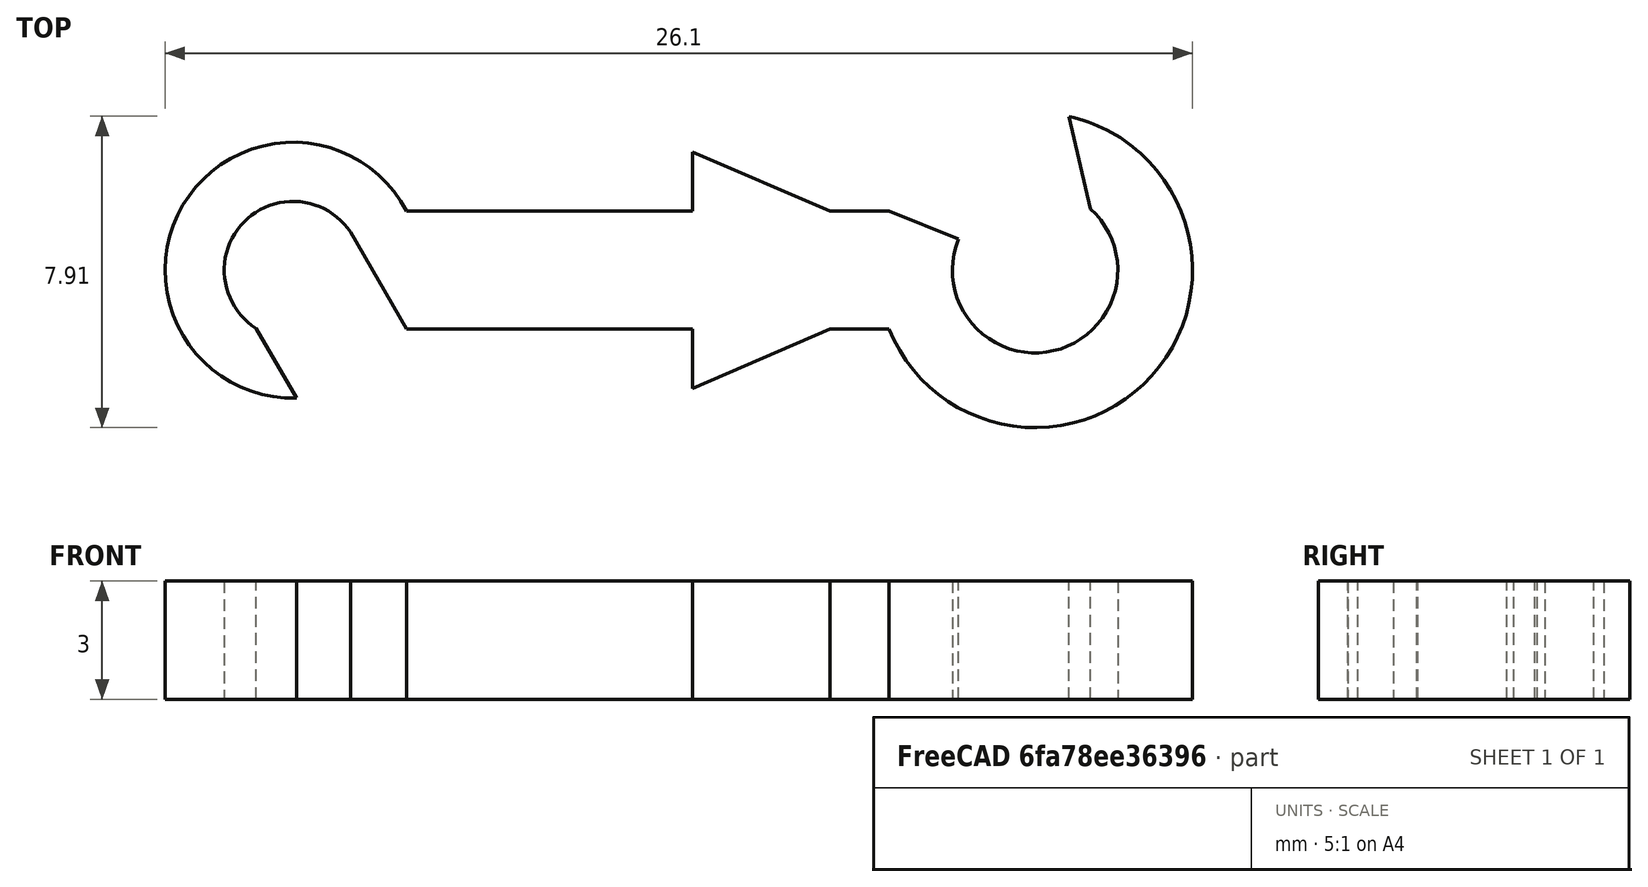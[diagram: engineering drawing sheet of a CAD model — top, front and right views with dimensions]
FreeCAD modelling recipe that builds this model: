
FCSTD DOCUMENT  (FreeCAD 0.20RUnknown)
Label: Haken01
License: All rights reserved
LicenseURL: http://en.wikipedia.org/wiki/All_rights_reserved
objects: Sketcher::SketchObject×1, PartDesign::Pad×1, PartDesign::Body×1
note: 4 computed .brp shape members not serialized (recipe doc carries the construction recipe); baked Part::Feature solids carry a one-line shape summary decoded from their .brp

FEATURE [Sketcher::SketchObject] Sketch
  FullyConstrained = true
  MapMode = 5
  Support = -> [XY_Plane]
  sketch-geometry (31):
    g0: Circle CenterX=0 CenterY=0 CenterZ=0 NormalX=0 NormalY=0 NormalZ=1 AngleXU=0 Radius=1.75
    g1: Circle CenterX=18.85 CenterY=0 CenterZ=0 NormalX=0 NormalY=0 NormalZ=1 AngleXU=0 Radius=2.1
    g2: LineSegment StartX=1.75 StartY=0 StartZ=0 EndX=16.75 EndY=0 EndZ=0
    g3: ArcOfCircle CenterX=18.85 CenterY=0 CenterZ=0 NormalX=0 NormalY=0 NormalZ=1 AngleXU=0 Radius=4 StartAngle=3.52599 EndAngle=7.12052
    g4: ArcOfCircle CenterX=18.85 CenterY=0 CenterZ=0 NormalX=0 NormalY=0 NormalZ=1 AngleXU=0 Radius=2.1 StartAngle=2.7572 EndAngle=7.12052
    g5: ArcOfCircle CenterX=0 CenterY=0 CenterZ=0 NormalX=0 NormalY=0 NormalZ=1 AngleXU=0 Radius=1.75 StartAngle=0.583388 EndAngle=4.14659
    g6: ArcOfCircle CenterX=0 CenterY=0 CenterZ=0 NormalX=0 NormalY=0 NormalZ=1 AngleXU=0 Radius=3.25 StartAngle=0.479729 EndAngle=4.73845
    g7: LineSegment StartX=18.85 StartY=0 StartZ=0 EndX=16.9032 EndY=0.7875 EndZ=0
    g8: LineSegment StartX=16.9032 StartY=0.7875 StartZ=0 EndX=15.1419 EndY=1.5 EndZ=0
    g9: LineSegment StartX=18.85 StartY=0 StartZ=0 EndX=20.2558 EndY=1.56001 EndZ=0
    g10: LineSegment StartX=20.2558 StartY=1.56001 StartZ=0 EndX=21.5278 EndY=2.97144 EndZ=0
    g11: LineSegment StartX=0 StartY=0 StartZ=0 EndX=-1.625 EndY=2.81458 EndZ=0
    g12: LineSegment StartX=2.88314 StartY=-1.5 StartZ=0 EndX=1.46055 EndY=0.963995 EndZ=0
    g13: LineSegment StartX=0.0846838 StartY=-3.2489 StartZ=0 EndX=-0.938159 EndY=-1.47728 EndZ=0
    g14: LineSegment StartX=2.88314 StartY=1.5 StartZ=0 EndX=2.88314 EndY=-1.5 EndZ=0
    g15: LineSegment StartX=15.1419 StartY=1.5 StartZ=0 EndX=15.1419 EndY=0 EndZ=0
    g16: LineSegment StartX=15.1419 StartY=0 StartZ=0 EndX=15.1419 EndY=-1.5 EndZ=0
    g17: LineSegment StartX=13.6419 StartY=1.5 StartZ=0 EndX=10.1419 EndY=3 EndZ=0
    g18: LineSegment StartX=10.1419 StartY=3 StartZ=0 EndX=10.1419 EndY=1.5 EndZ=0
    g19: LineSegment StartX=13.6419 StartY=-1.5 StartZ=0 EndX=10.1419 EndY=-3 EndZ=0
    g20: LineSegment StartX=10.1419 StartY=-3 StartZ=0 EndX=10.1419 EndY=-1.5 EndZ=0
    g21: LineSegment StartX=10.1419 StartY=1.5 StartZ=0 EndX=10.1419 EndY=-1.5 EndZ=0
    g22: LineSegment StartX=13.6419 StartY=1.5 StartZ=0 EndX=13.6419 EndY=-1.5 EndZ=0
    g23: LineSegment StartX=10.1419 StartY=1.5 StartZ=0 EndX=2.88314 EndY=1.5 EndZ=0
    g24: LineSegment StartX=15.1419 StartY=1.5 StartZ=0 EndX=13.6419 EndY=1.5 EndZ=0
    g25: LineSegment StartX=13.6419 StartY=1.5 StartZ=0 EndX=10.1419 EndY=1.5 EndZ=0
    g26: LineSegment StartX=10.1419 StartY=-1.5 StartZ=0 EndX=2.88314 EndY=-1.5 EndZ=0
    g27: LineSegment StartX=15.1419 StartY=-1.5 StartZ=0 EndX=13.6419 EndY=-1.5 EndZ=0
    g28: LineSegment StartX=13.6419 StartY=-1.5 StartZ=0 EndX=10.1419 EndY=-1.5 EndZ=0
    g29: LineSegment StartX=20.2558 StartY=1.56001 StartZ=0 EndX=19.7154 EndY=3.90525 EndZ=0
    g30: ArcOfCircle CenterX=18.85 CenterY=0 CenterZ=0 NormalX=0 NormalY=0 NormalZ=1 AngleXU=0 Radius=4 StartAngle=0.837334 EndAngle=1.35271
  constraints (89):
    c: Diameter(g0) = 3.5
    c: PointOnObject(g1,g-1)
    c: PointOnObject(g2,g0)
    c: PointOnObject(g2,g1)
    c: Horizontal(g2)
    c: PointOnObject(g2,g-1)
    c: DistanceX(g2,g2) = 15
    c: Coincident(g27,g3)
    c: Coincident(g4,g3)
    c: Coincident(g5,g0)
    c: Equal(g1,g4)
    c: Equal(g0,g5)
    c: Coincident(g6,g5)
    c: Coincident(g6,g23)
    c: Coincident(g3,g1)
    c: Coincident(g7,g3)
    c: Coincident(g8,g24)
    c: Coincident(g7,g8)
    c: Parallel(g7,g8)
    c: Coincident(g9,g3)
    c: Coincident(g9,g10)
    c: Parallel(g10,g9)
    c: Angle(g9,g7) = 1.91986
    c: Diameter(g6) = 6.5
    c: Diameter(g3) = 8
    c: DistanceY(g26,g23) = 3
    c: Coincident(g3,g10)
    c: Coincident(g4,g9)
    c: Coincident(g4,g7)
    c: Coincident(g11,g5)
    c: Coincident(g12,g26)
    c: Parallel(g11,g13)
    c: Parallel(g12,g11)
    c: Coincident(g14,g23)
    c: Coincident(g14,g26)
    c: Vertical(g14)
    c: Distance(g13,g26) = 3.3
    c: Coincident(g5,g13)
    c: Coincident(g6,g13)
    c: PointOnObject(g11,g6)
    c: PointOnObject(g15,g2)
    c: Coincident(g16,g15)
    c: Coincident(g16,g3)
    c: Vertical(g16)
    c: Vertical(g15)
    c: Equal(g15,g16)
    c: Coincident(g5,g12)
    c: Coincident(g5,g-1)
    c: Diameter(g4) = 4.2
    c: Coincident(g17,g18)
    c: Vertical(g18)
    c: Coincident(g19,g20)
    c: Vertical(g20)
    c: Coincident(g21,g18)
    c: Coincident(g21,g20)
    c: Coincident(g22,g17)
    c: Coincident(g22,g19)
    c: Vertical(g21)
    c: Vertical(g22)
    c: Equal(g18,g20)
    c: DistanceX(g19,g3) = 1.5
    c: DistanceX(g20,g19) = 3.5
    c: DistanceY(g20,g20) = 1.5
    c: Coincident(g25,g23)
    c: Horizontal(g23)
    c: PointOnObject(g18,g23)
    c: Coincident(g24,g25)
    c: Horizontal(g24)
    c: Horizontal(g25)
    c: PointOnObject(g15,g24)
    c: PointOnObject(g17,g24)
    c: Coincident(g28,g26)
    c: Horizontal(g26)
    c: PointOnObject(g20,g26)
    c: Coincident(g27,g28)
    c: Horizontal(g27)
    c: Horizontal(g28)
    c: PointOnObject(g19,g27)
    c: PointOnObject(g23,g18)
    c: PointOnObject(g26,g20)
    c: PointOnObject(g27,g19)
    c: PointOnObject(g24,g17)
    c: Equal(g24,g27)
    c: Angle(g26,g12) = 2.0944
    c: Coincident(g29,g4)
    c: Coincident(g30,g3)
    c: Coincident(g30,g3)
    c: Coincident(g30,g29)
    c: Angle(g10,g29) = 0.959931
FEATURE [PartDesign::Pad] Pad
  Direction = (0,0,1)
  Length = 3
  Length2 = 10
  Profile = -> Sketch
  ReferenceAxis = -> Sketch [N_Axis]
  Type = 0
FEATURE [PartDesign::Body] Body
  Group = -> [Sketch,Pad]
  Origin = -> Origin
  Tip = -> Pad
